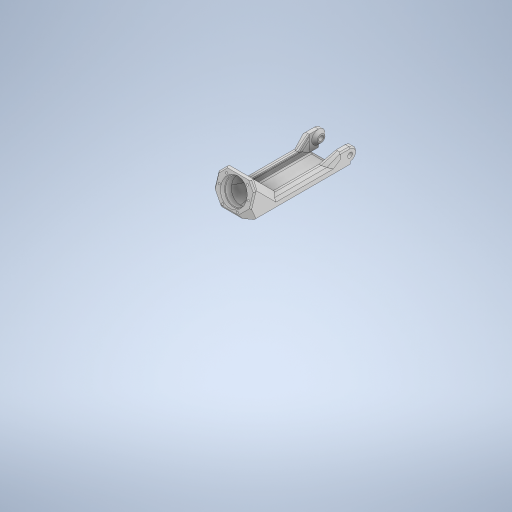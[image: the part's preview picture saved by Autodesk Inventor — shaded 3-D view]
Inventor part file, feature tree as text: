
AUTODESK INVENTOR PART (.ipt)
format: ipt  version: 2023.4 (Build 274418000, 418)  size: 1,138,176 bytes
history: native  units: mm
features: extrude x17, chamfer x16, other x8, sketch x7, projected_geometry x6, loft x5, plane x2, mirror x1
ambient origin geometry x8: Origin, YZ Plane, XZ Plane, XY Plane, X Axis, Y Axis, Z Axis, Center Point
bodies: Solid1 (feature_tree)
feature tree (62):
  extrude  "Extrusion1"  Depth=12.0mm
  extrude  "Extrusion2"  Depth=60.0mm
  chamfer  "Chamfer3"  Distance=8.0mm
  chamfer  "Chamfer4"  Distance=5.0mm
  extrude  "Extrusion3"  Depth=4.0mm
  extrude  "Extrusion4"  Depth=4.0mm
  chamfer  "Chamfer5"  Distance=3.0mm
  extrude  "Extrusion5"  Depth=6.0mm
  loft  "Loft1"
  loft  "Loft2"
  chamfer  "Chamfer6"  Distance=6.0mm
  extrude  "Extrusion6"  TaperAngle=0.0deg  [1 undecoded]
  extrude  "Extrusion7"  Depth=1.0mm
  chamfer  "Chamfer7"  Distance=1.0mm
  chamfer  "Chamfer8"  Distance=1.0mm
  plane  "Work Plane1"
  loft  "Loft3"
  plane  "Work Plane2"
  loft  "Loft4"
  extrude  "Extrusion8"  Depth=0.7mm
  extrude  "Extrusion9"  Depth=38.4mm
  extrude  "Extrusion10"  Depth=2.0mm TaperAngle=45.0deg
  extrude  "Extrusion11"  Depth=2.0mm TaperAngle=45.0deg
  loft  "Loft5"
  chamfer  "Chamfer9"  [1 undecoded]
  chamfer  "Chamfer10"  Distance=26.0mm
  chamfer  "Chamfer11"  Distance=60.0mm
  chamfer  "Chamfer12"  Distance=8.0mm
  chamfer  "Chamfer13"  Distance=8.0mm
  extrude  "Extrusion12"  Depth=26.0mm TaperAngle=0.0deg
  extrude  "Extrusion14"  Depth=2.0mm TaperAngle=45.0deg
  extrude  "Extrusion15"  Depth=0.1mm TaperAngle=0.0deg
  extrude  "Extrusion16"  TaperAngle=0.0deg  [1 undecoded]
  chamfer  "Chamfer14"  Angle=90.0deg  [1 undecoded]
  chamfer  "Chamfer15"  Angle=90.0deg  [1 undecoded]
  chamfer  "Chamfer16"  Angle=90.0deg  [1 undecoded]
  extrude  "Extrusion17"  Depth=2.0mm TaperAngle=45.0deg
  extrude  "Extrusion18"  Depth=15.0mm
  mirror  "Mirror1"
  chamfer  "Chamfer17"  [1 undecoded]
  chamfer  "Chamfer18"  Distance=8.1mm
  sketch  "Sketch1"  dims[d8=97.0mm d9=0.0mm d17=12.0mm]
  sketch  "Sketch2"  dims[d18=37.0mm d20=60.0mm]
  projected_geometry  "Projected Loop1"
  projected_geometry  "Projected Loop2"
  other  "Edges1"
  other  "Edges2"
  other  "Edges3"
  other  "Edges4"
  sketch  "Sketch6"  dims[d21=11.5mm]
  projected_geometry  "Projected Loop3"
  other  "Edges5"
  projected_geometry  "Projected Loop4"
  other  "Edges6"
  projected_geometry  "Projected Loop5"
  sketch  "Sketch11"  dims[d22=2.0mm]
  projected_geometry  "Projected Loop6"
  other  "Edges7"
  other  "Edges8"
  sketch  "Sketch15"  dims[d23=8.0mm]
  sketch  "Sketch20"  dims[d24=8.0mm]
  sketch  "Sketch21"  dims[d25=8.0mm d26=8.0mm d27=5.0mm d28=4.0mm d29=4.0mm d30=3.0mm d31=6.0mm d32=6.0mm d33=6.0mm d34=6.0mm d35=0.0mm d36=0.0mm d37=1.0mm d38=1.0mm d39=1.0mm d40=1.0mm d41=0.7mm d42=0.7mm d43=38.4mm d44=2.0mm d45=2.0mm d46=45.0deg d47=2.0mm d48=2.0mm d49=45.0deg d50=27.0mm d51=0.0mm d52=0.0mm d53=26.0mm d54=60.0mm d55=8.0mm d56=8.0mm d57=26.0mm d58=0.0mm d59=2.0mm d60=2.0mm d61=45.0deg d62=0.1mm d63=0.0mm d64=0.0mm d65=90.0deg d66=0.0mm d67=90.0deg d68=0.0mm d69=90.0deg d70=0.0mm d71=90.0deg d72=2.0mm d73=2.0mm d74=45.0deg d77=15.0mm d78=0.0mm d79=0.0mm d80=8.1mm d81=0.0mm d82=0.0mm d83=2.0mm d84=2.0mm d85=45.0deg d86=2.0mm d87=2.0mm d88=45.0deg d89=5.0mm d90=0.0mm d91=90.0deg d92=0.0mm d93=90.0deg d94=5.0mm d95=0.0mm d96=90.0deg d97=0.0mm d98=90.0deg d99=10.0mm d100=0.0mm d101=0.0mm d102=0.0mm d103=56.0mm d104=50.0mm d105=45.0deg d106=0.0mm d107=0.0mm d108=10.0mm d109=0.0mm d110=42.0mm d111=21.0mm d112=7.0mm d113=42.0mm d114=56.0mm d115=0.0mm d116=42.1mm d117=42.0mm d118=21.0mm d119=60.0mm d120=30.0mm d121=10.0mm d122=0.0mm d123=39.0mm d124=10.0mm d125=0.0mm d126=0.0mm d127=0.0mm d129=0.0mm d130=0.0mm d131=0.0mm d132=90.0deg d133=0.0mm d134=90.0deg d135=10.0mm d136=2.0mm d137=45.0deg d138=2.0mm d139=2.0mm d140=45.0deg d141=14.0mm d142=2.0mm d143=45.0deg d144=6.0mm d145=2.0mm d146=45.0deg d147=2.0mm d148=2.0mm d149=45.0deg d150=3.2mm d151=4.0mm d152=0.0mm d153=10.0mm d154=0.0mm d155=60.0mm d157=360.0deg d167=42.2mm d168=97.0mm d169=0.0mm d170=13.0mm d171=4.5mm d172=0.0mm d173=4.5mm d174=0.0mm d175=4.5mm d176=2.0mm d177=45.0deg d178=4.5mm d179=2.0mm d180=45.0deg d181=0.5mm d182=2.0mm d183=45.0deg d184=80.0mm d186=360.0deg d188=8.0mm d189=0.0mm d190=0.0mm d191=0.0mm d192=6.0mm d193=2.0mm d194=45.0deg d195=6.0mm d196=2.0mm d197=45.0deg]
note: 7 required parameter values undecoded (feature->parameter linkage not recoverable at this tier; creation-order binding heuristic only, values carry confidence <= 0.55)
